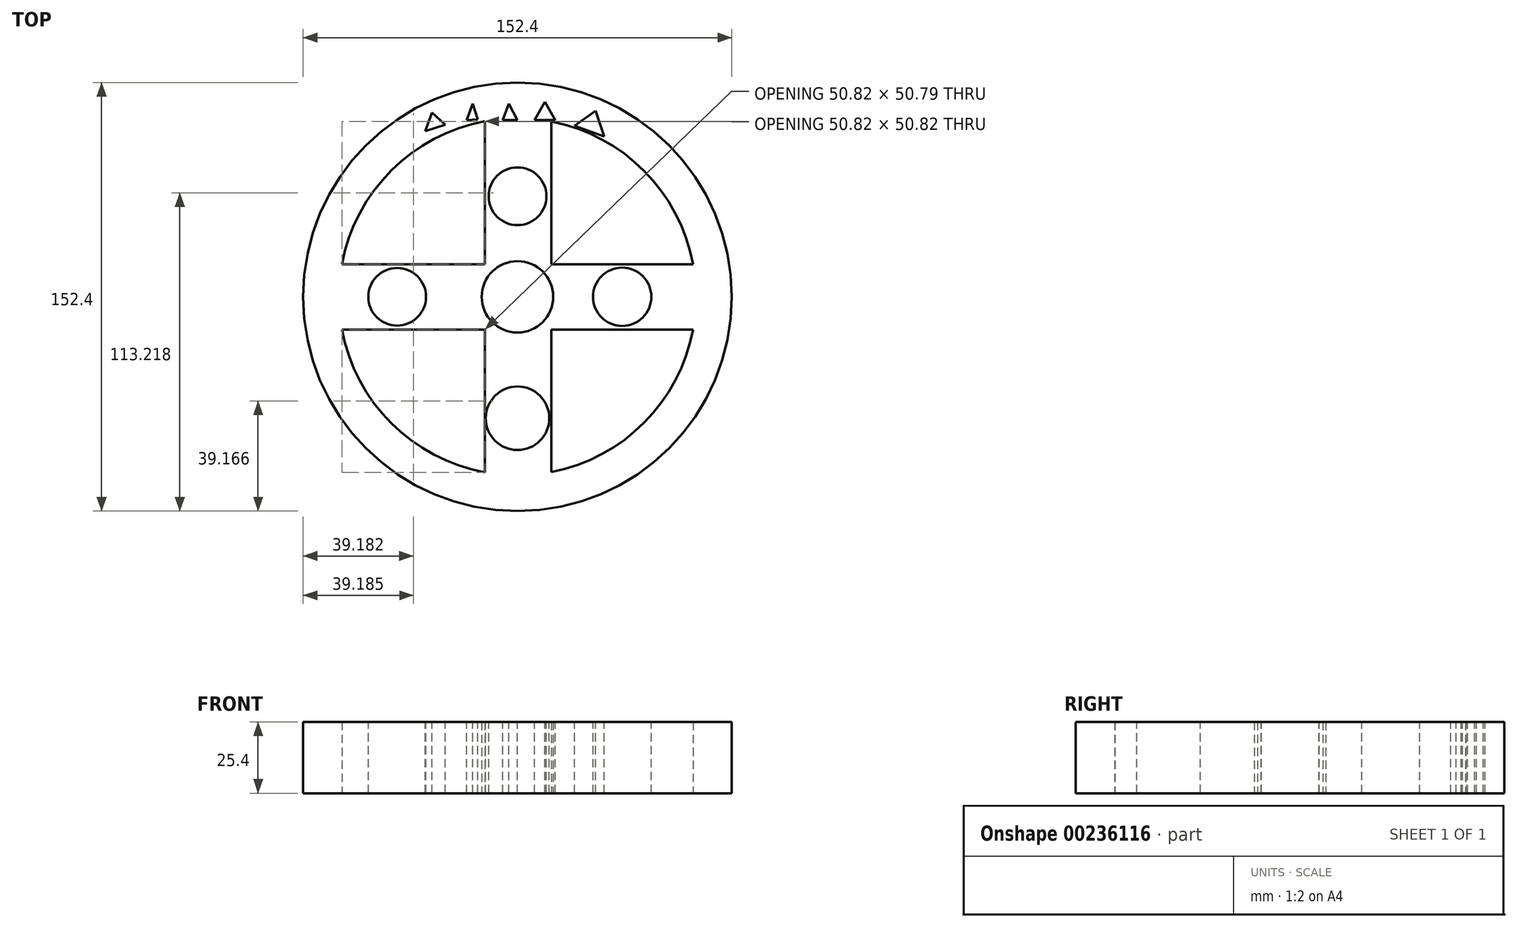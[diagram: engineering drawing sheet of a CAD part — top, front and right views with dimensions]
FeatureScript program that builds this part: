
annotation { "Feature Type Name" : "Feature", "Feature Type Description" : "" }
export const myFeature = defineFeature(function(context is Context, id is Id, definition is map)
    precondition{}
    {
        {
            var Q0;
            Q0=qCreatedBy(makeId("Top.planeOp"),FACE);
            var sketch = newSketch(context, id + "F0", { "sketchPlane" : qUnion([Q0])});
            skCircle(sketch, "E0", {"center": v(0, 0) * mm, "radius": 76.2 * mm});
            skCircle(sketch, "E1", {"center": v(0, 0) * mm, "radius": 12.7 * mm});
            skArc(sketch, "E2", {"start": v(-62.42, -11.64) * mm, "mid": v(-44.9, -44.91) * mm, "end": v(-11.6, -62.43) * mm});
            skLineSegment(sketch, "E3", {"start": v(0, 0) * mm, "end": v(0, 63.5) * mm});
            skLineSegment(sketch, "E4", {"start": v(0, 0) * mm, "end": v(0, -63.5) * mm});
            skLineSegment(sketch, "E5", {"start": v(12.08, 62.34) * mm, "end": v(12.08, 11.6) * mm});
            skLineSegment(sketch, "E6", {"start": v(-11.6, 62.43) * mm, "end": v(-11.6, 11.6) * mm});
            skLineSegment(sketch, "E7", {"start": v(-63.5, 0) * mm, "end": v(63.5, 0) * mm});
            skLineSegment(sketch, "E8", {"start": v(-62.43, 11.6) * mm, "end": v(-11.6, 11.6) * mm});
            skLineSegment(sketch, "E9", {"start": v(-62.42, -11.64) * mm, "end": v(-11.6, -11.64) * mm});
            skPoint(sketch, "E10", {"position": v(-12.01, 75.25) * mm});
            skPoint(sketch, "E11", {"position": v(12.01, 75.25) * mm});
            skLineSegment(sketch, "E12.trimOffspring", {"start": v(12.08, -75.24) * mm, "end": v(12.08, -76.2) * mm});
            skPoint(sketch, "E13.orphan", {"position": v(0, -76.2) * mm});
            skPoint(sketch, "E14.orphan", {"position": v(-76.2, 0) * mm});
            skLineSegment(sketch, "E15.trimOffspring", {"start": v(12.08, -11.64) * mm, "end": v(12.08, -62.34) * mm});
            skLineSegment(sketch, "E16.trimOffspring", {"start": v(12.08, 11.6) * mm, "end": v(62.43, 11.6) * mm});
            skLineSegment(sketch, "E17.trimOffspring", {"start": v(12.08, -11.64) * mm, "end": v(62.42, -11.64) * mm});
            skLineSegment(sketch, "E18.trimOffspring", {"start": v(-11.6, -11.64) * mm, "end": v(-11.6, -62.43) * mm});
            skArc(sketch, "E19.trimOffspring", {"start": v(62.43, 11.6) * mm, "mid": v(45.07, 44.73) * mm, "end": v(12.08, 62.34) * mm});
            skArc(sketch, "E20.trimOffspring", {"start": v(-11.6, 62.43) * mm, "mid": v(-44.9, 44.9) * mm, "end": v(-62.43, 11.6) * mm});
            skArc(sketch, "E21.trimOffspring", {"start": v(12.08, -62.34) * mm, "mid": v(45.06, -44.74) * mm, "end": v(62.42, -11.64) * mm});
            skSolve(sketch);
        }
        {
            var Q0;
            Q0 = qSketchRegion(id + "F0", true);
            extrude(context, id + "F1", {"entities" : qUnion([Q0]), "endBound" : BoundingType.SYMMETRIC, "depth" : 25.4 * mm});
        }
        {
            var Q0;
            Q0=qCreatedBy(makeId("Top.planeOp"),FACE);
            var sketch = newSketch(context, id + "F2", { "sketchPlane" : qUnion([Q0])});
            skArc(sketch, "E22", {"start": v(-45.07, 22.36) * mm, "mid": v(-34.78, 15.1) * mm, "end": v(-24.8, 22.77) * mm});
            skCircle(sketch, "E23", {"center": v(-39.48, 31.04) * mm, "radius": 3.37 * mm});
            skCircle(sketch, "E24", {"center": v(-28.73, 30.84) * mm, "radius": 3.37 * mm});
            skLineSegment(sketch, "E25", {"start": v(-30.39, 65.57) * mm, "end": v(-32.87, 58.96) * mm});
            skLineSegment(sketch, "E26", {"start": v(-32.87, 58.96) * mm, "end": v(-25.63, 61.23) * mm});
            skLineSegment(sketch, "E27", {"start": v(-25.63, 61.23) * mm, "end": v(-30.39, 65.57) * mm});
            skLineSegment(sketch, "E28", {"start": v(-15.91, 68.67) * mm, "end": v(-18.09, 62.88) * mm});
            skLineSegment(sketch, "E29", {"start": v(-15.91, 68.67) * mm, "end": v(-14.16, 63.08) * mm});
            skLineSegment(sketch, "E30", {"start": v(-18.09, 62.88) * mm, "end": v(-14.16, 63.08) * mm});
            skLineSegment(sketch, "E31", {"start": v(-3.1, 68.67) * mm, "end": v(-5.27, 62.88) * mm});
            skLineSegment(sketch, "E32", {"start": v(-5.27, 62.88) * mm, "end": v(0, 62.88) * mm});
            skLineSegment(sketch, "E33", {"start": v(-3.1, 68.67) * mm, "end": v(0, 62.88) * mm});
            skLineSegment(sketch, "E34", {"start": v(6, 62.88) * mm, "end": v(13.44, 62.88) * mm});
            skLineSegment(sketch, "E35", {"start": v(6, 62.88) * mm, "end": v(9.72, 69.3) * mm});
            skPoint(sketch, "E35.endSnap0", {"position": v(9.72, 62.88) * mm});
            skLineSegment(sketch, "E36", {"start": v(9.72, 69.3) * mm, "end": v(13.44, 62.88) * mm});
            skLineSegment(sketch, "E37", {"start": v(27.7, 66.2) * mm, "end": v(20.27, 60.82) * mm});
            skLineSegment(sketch, "E38", {"start": v(20.27, 60.82) * mm, "end": v(30.8, 57.1) * mm});
            skLineSegment(sketch, "E39", {"start": v(27.7, 66.2) * mm, "end": v(30.8, 57.1) * mm});
            skLineSegment(sketch, "E40", {"start": v(48.38, 54.2) * mm, "end": v(40.73, 57.1) * mm});
            skLineSegment(sketch, "E41", {"start": v(40.73, 56.68) * mm, "end": v(40.73, 49.86) * mm});
            skLineSegment(sketch, "E42", {"start": v(42.39, 50.27) * mm, "end": v(48.38, 54.2) * mm});
            skArc(sketch, "E43", {"start": v(21.5, 22.95) * mm, "mid": v(31.74, 17.48) * mm, "end": v(41.97, 22.95) * mm});
            skCircle(sketch, "E44", {"center": v(25.22, 32.25) * mm, "radius": 3.52 * mm});
            skCircle(sketch, "E45", {"center": v(38.66, 32.05) * mm, "radius": 3.51 * mm});
            skArc(sketch, "E46", {"start": v(-41.35, -38.66) * mm, "mid": v(-33.06, -43.62) * mm, "end": v(-23.98, -40.32) * mm});
            skCircle(sketch, "E47", {"center": v(-37.42, -32.44) * mm, "radius": 3.75 * mm});
            skCircle(sketch, "E48", {"center": v(-26.05, -32.44) * mm, "radius": 3.5 * mm});
            skArc(sketch, "E49", {"start": v(17.37, -41.97) * mm, "mid": v(27.4, -46.83) * mm, "end": v(37.21, -41.56) * mm});
            skCircle(sketch, "E50", {"center": v(20.67, -34.58) * mm, "radius": 3.9 * mm});
            skCircle(sketch, "E51", {"center": v(34.11, -34.58) * mm, "radius": 3.94 * mm});
            skCircle(sketch, "E52", {"center": v(37.21, 0) * mm, "radius": 10.37 * mm});
            skCircle(sketch, "E53", {"center": v(-42.8, 0) * mm, "radius": 10.26 * mm});
            skCircle(sketch, "E54", {"center": v(0, 35.77) * mm, "radius": 10.26 * mm});
            skCircle(sketch, "E55", {"center": v(0, -43.2) * mm, "radius": 11.3 * mm});
            skSolve(sketch);
        }
        {
            var Q0;
            Q0 = qSketchRegion(id + "F2", true);
            extrude(context, id + "F3", {"entities" : qUnion([Q0]), "operationType" : NewBodyOperationType.REMOVE, "endBound" : BoundingType.SYMMETRIC, "oppositeDirection" : true, "depth" : 25.4 * mm});
        }
    });
